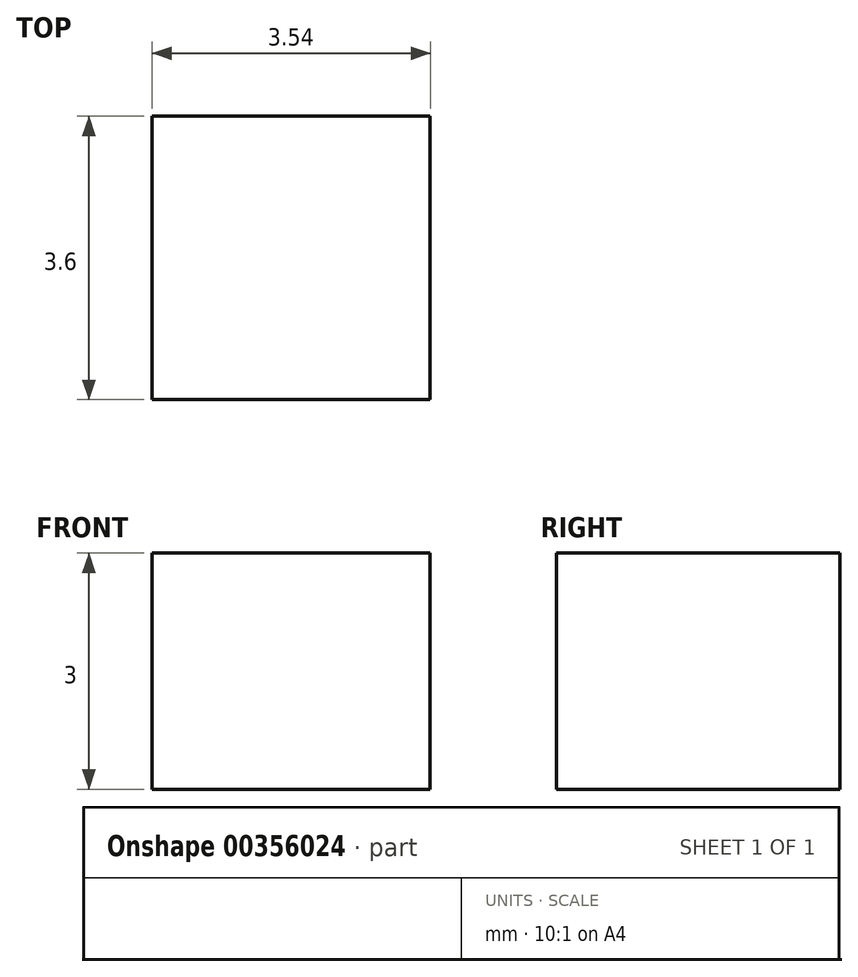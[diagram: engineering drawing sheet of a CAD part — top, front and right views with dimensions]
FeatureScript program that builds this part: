
annotation { "Feature Type Name" : "Feature", "Feature Type Description" : "" }
export const myFeature = defineFeature(function(context is Context, id is Id, definition is map)
    precondition{}
    {
        {
            var Q0;
            Q0=qCreatedBy(makeId("Top.planeOp"),FACE);
            var sketch = newSketch(context, id + "F0", { "sketchPlane" : qUnion([Q0])});
            skLineSegment(sketch, "E0.bottom", {"start": v(1.77, -1.8) * mm, "end": v(-1.77, -1.8) * mm});
            skLineSegment(sketch, "E0.top", {"start": v(1.77, 1.8) * mm, "end": v(-1.77, 1.8) * mm});
            skLineSegment(sketch, "E0.left", {"start": v(1.77, -1.8) * mm, "end": v(1.77, 1.8) * mm});
            skLineSegment(sketch, "E0.right", {"start": v(-1.77, -1.8) * mm, "end": v(-1.77, 1.8) * mm});
            skPoint(sketch, "E0.middle", {"position": v(0, 0) * mm});
            skSolve(sketch);
        }
        {
            var Q0;
            Q0=makeQuery(id+"F0.imprint","IMPRINT",FACE,{"disambiguationData":[TD([[makeQuery(id+"F0.imprint","IMPRINT",EDGE,{"derivedFrom":sQuery(id+"F0.wireOp",EDGE,"E0.bottom")}),-1.0]])]});
            extrude(context, id + "F1", {"entities" : qUnion([Q0]), "depth" : 3 * mm});
        }
    });
